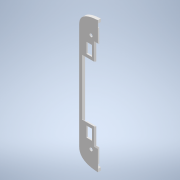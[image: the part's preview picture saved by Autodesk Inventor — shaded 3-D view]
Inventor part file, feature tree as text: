
AUTODESK INVENTOR PART (.ipt)
format: ipt  version: 2022 (Build 260153000, 153)  size: 337,408 bytes
history: native  units: mm
features: other x6, extrude x6, sketch x6, reference x6, projected_geometry x4, chamfer x1, mirror x1
ambient origin geometry x8: Origin, YZ Plane, XZ Plane, XY Plane, X Axis, Y Axis, Z Axis, Center Point
bodies: Body1 (feature_tree)
feature tree (30):
  other  "Твердое тело1"
  extrude  "Выдавливание1"  Depth=3.0mm
  extrude  "Выдавливание3"  Depth=3.0mm TaperAngle=0.0deg
  extrude  "Выдавливание4"  Depth=0.3mm
  extrude  "Выдавливание5"  Depth=0.4mm TaperAngle=0.0deg
  extrude  "Выдавливание7"  Depth=3.2mm
  extrude  "Выдавливание8"  Depth=3.2mm
  chamfer  "Фаска3"  Distance=1.0mm
  mirror  "Зеркальное отражение1"
  sketch  "Эскиз1"
  reference  "Ссылка1"
  reference  "Ссылка2"
  sketch  "Эскиз3"
  projected_geometry  "Спроецированная петля2"
  reference  "Ссылка4"
  reference  "Ссылка5"
  sketch  "Эскиз4"
  reference  "Ссылка6"
  sketch  "Эскиз5"
  projected_geometry  "Спроецированная петля3"
  sketch  "Эскиз7"
  projected_geometry  "Спроецированная петля6"
  sketch  "Эскиз8"
  projected_geometry  "Спроецированная петля7"
  reference  "Ссылка7"
  other  "<userpath>\Documents\Git\MZCAT_2024\MZCAT_4.iam"
  other  "MZCAT_4.iam"
  other  "CAT_protector:1"
  other  "magazine_fixator:1"
  other  "left_back_cup:1"
